# Revit family: FMS2_63_UN_Surface-mounted_ETK
name_source: partatom
category: Lighting Fixtures
units: mm (PartAtom-declared; Revit-internal decimal feet)

## family parameters
Always vertical = Yes
Cut with Voids When Loaded = No
Light Source = No
OmniClass Number = 23.80.70.11.14.11
OmniClass Title = Downlights
Part Type = Normal
Room Calculation Point = Yes
Round Connector Dimension = Use Diameter
Shared = No
Work Plane-Based = No

## types (2) — shared parameters
Apparent Load = 18 VA
Assembly Code = 63.0
Bundle = 110°
Description = Surface Mounted
IfcExportAs = IfcLightFixtureType
IfcExportType = USERDEFINED
Lamp = LED
Luminaire_Body_Material = PPS Plastic
Manufacturer = ETK licht B.V.
Type Comments = IP20
URL = https://www.etk.nl
Voltage = 230 V
Wattage Comments = 18W

## per-type parameters (varying)
| type | Light Source | Model |
| FMS.2100.10 - 260x260 / 18W / 1120lm / 3000K | FMS.2 - Lightsource : FMS.2100.10 - 260x260 / 18W / 1120lm / 3000K | FMS.2 |
| FMS.2100.10N - 260x260 / 18W / 1120lm / 3000K | FMS.2 - Lightsource : FMS.2100.10N - 260x260 / 18W / 1120lm / 3000K | FMK.1 |

## geometry (parser evidence)
native form markers: Sweep x9
no freeform markers — native parametric forms only
